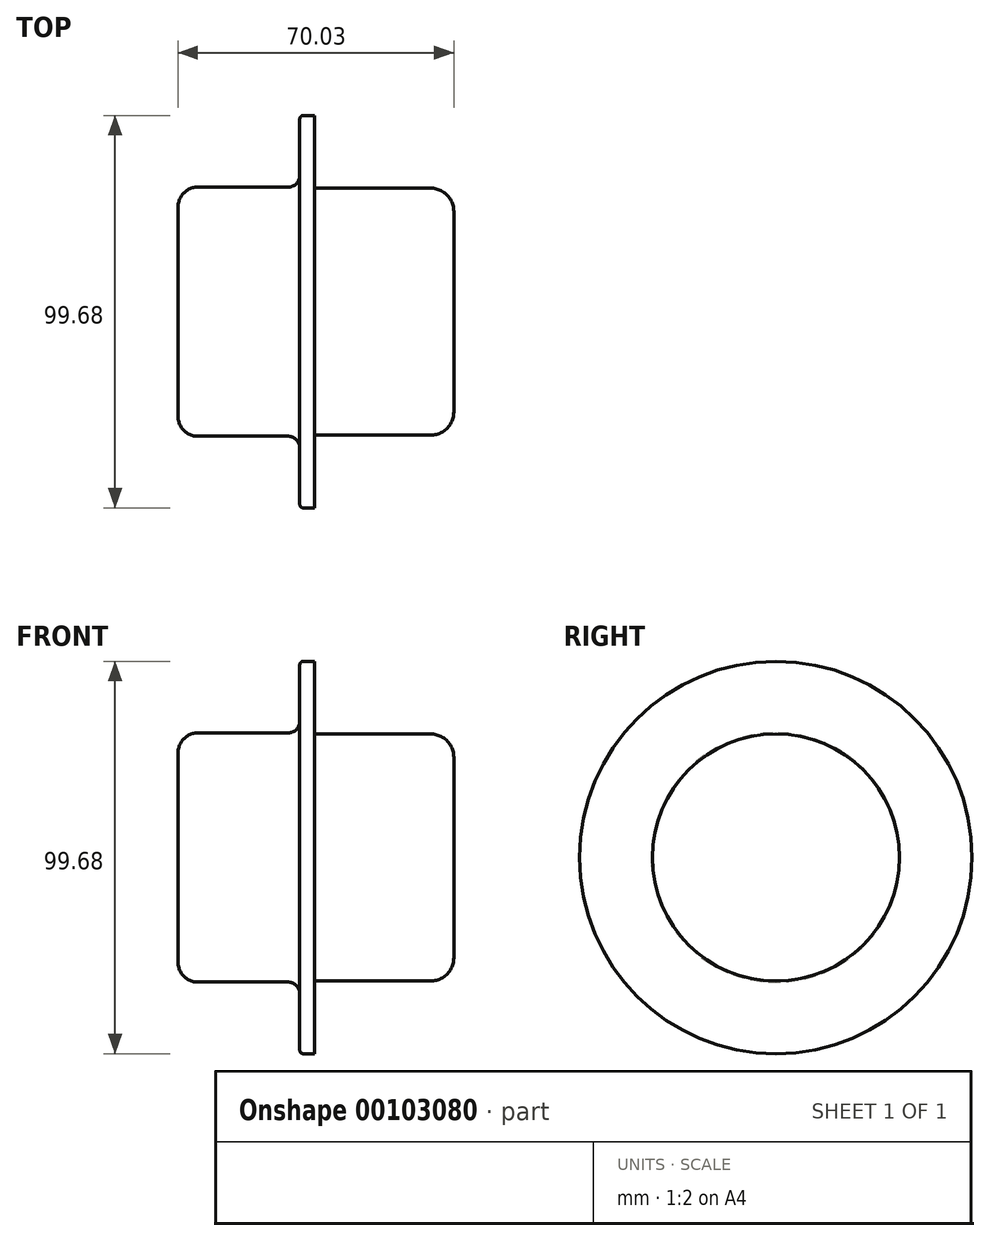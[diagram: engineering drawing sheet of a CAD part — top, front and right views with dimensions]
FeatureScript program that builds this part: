
annotation { "Feature Type Name" : "Feature", "Feature Type Description" : "" }
export const myFeature = defineFeature(function(context is Context, id is Id, definition is map)
    precondition{}
    {
        {
            var Q0;
            Q0=qCreatedBy(makeId("Front.planeOp"),FACE);
            var sketch = newSketch(context, id + "F0", { "sketchPlane" : qUnion([Q0])});
            skLineSegment(sketch, "E0", {"start": v(-42.99, 0) * mm, "end": v(-42.99, 26.67) * mm});
            skLineSegment(sketch, "E1", {"start": v(-38, 31.65) * mm, "end": v(-15.05, 31.65) * mm});
            skLineSegment(sketch, "E2", {"start": v(-12.09, 34.61) * mm, "end": v(-12.09, 49) * mm});
            skLineSegment(sketch, "E3", {"start": v(-11.24, 49.84) * mm, "end": v(-8.35, 49.84) * mm});
            skLineSegment(sketch, "E4", {"start": v(-8.35, 49.84) * mm, "end": v(-8.35, 31.4) * mm});
            skLineSegment(sketch, "E5", {"start": v(-8.35, 31.4) * mm, "end": v(21.1, 31.4) * mm});
            skLineSegment(sketch, "E6", {"start": v(27.04, 25.47) * mm, "end": v(27.04, 0) * mm});
            skLineSegment(sketch, "E7", {"start": v(27.04, 0) * mm, "end": v(-42.99, 0) * mm});
            skPoint(sketch, "E8.visualSharp", {"position": v(-42.99, 31.65) * mm});
            skArc(sketch, "E8.filletArc", {"start": v(-38, 31.65) * mm, "mid": v(-41.53, 30.19) * mm, "end": v(-42.99, 26.67) * mm});
            skPoint(sketch, "E9.visualSharp", {"position": v(27.04, 31.4) * mm});
            skArc(sketch, "E9.filletArc", {"start": v(27.04, 25.47) * mm, "mid": v(25.3, 29.66) * mm, "end": v(21.1, 31.4) * mm});
            skPoint(sketch, "E10.visualSharp", {"position": v(-12.09, 49.84) * mm});
            skArc(sketch, "E10.filletArc", {"start": v(-11.24, 49.84) * mm, "mid": v(-11.84, 49.6) * mm, "end": v(-12.09, 49) * mm});
            skPoint(sketch, "E11.visualSharp", {"position": v(-12.09, 31.65) * mm});
            skArc(sketch, "E11.filletArc", {"start": v(-15.05, 31.65) * mm, "mid": v(-12.96, 32.52) * mm, "end": v(-12.09, 34.61) * mm});
            skSolve(sketch);
        }
        {
            var Q0;
            Q0 = qSketchRegion(id + "F0", true);
            var Q1;
            Q1=sQuery(id+"F0.wireOp",EDGE,"E7");
            revolve(context, id + "F1", {"entities" : qUnion([Q0]), "axis" : qUnion([Q1]), "revolveType" : RevolveType.FULL});
        }
    });
